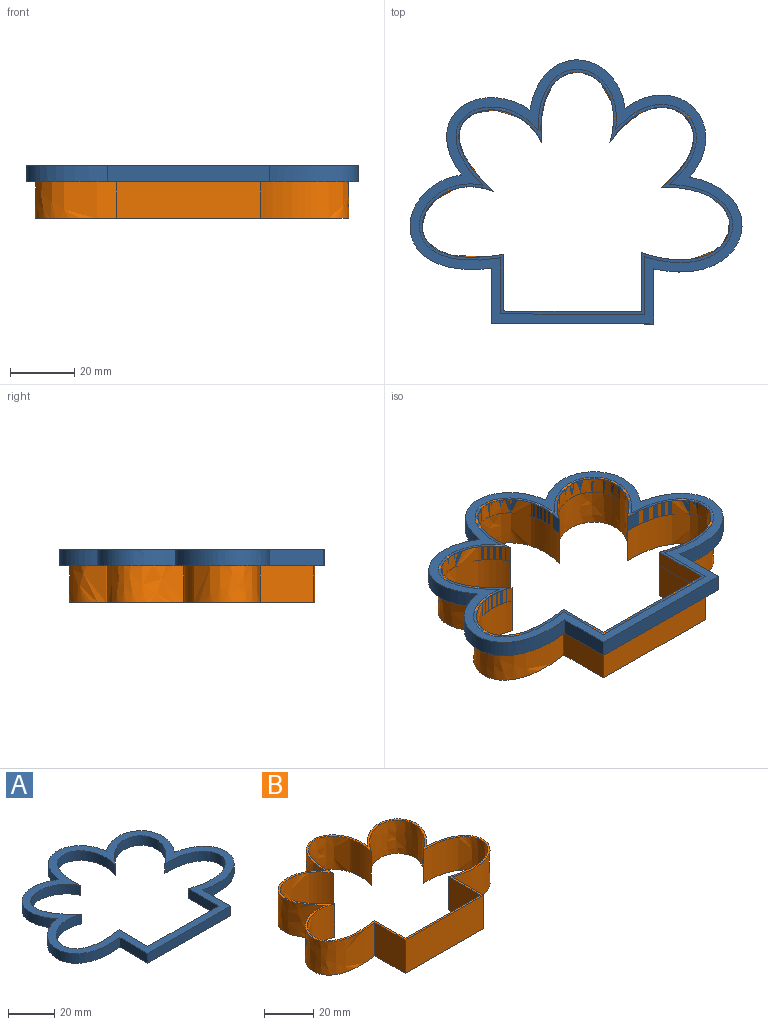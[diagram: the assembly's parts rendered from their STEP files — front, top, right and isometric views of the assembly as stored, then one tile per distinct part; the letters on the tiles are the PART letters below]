
ASSEMBLY  parts=2 mates=1
PART A: 18 faces, bbox 107.6x83.7x5.1 mm
  f0: plane 107.59x83.71mm, normal (0,0,1), area 1318.5mm2, adj f2,f3,f4,f5,f6,f7,f8,f9
  f1: plane 107.59x83.71mm, normal (0,0,-1), area 1318.5mm2, adj f2,f3,f4,f5,f6,f7,f8,f9
  f2: extruded ~29.44x25.38mm, area 290mm2, adj f0,f1,f3,f9
  f3: plane 17.02x5.08mm, normal (-1,0,0), area 86.4mm2, adj f0,f1,f2,f4
  f4: plane 50.51x5.08mm, normal (-0.01,-1,0), area 256.6mm2, adj f0,f1,f3,f5
  f5: plane 17.19x5.08mm, normal (1,0,0), area 87.3mm2, adj f0,f1,f4,f6
  f6: extruded ~29.53x27.52mm, area 300.9mm2, adj f0,f1,f5,f7
  f7: extruded ~25.58x25.16mm, area 239.9mm2, adj f0,f1,f6,f8
  f8: extruded ~29.6x15.62mm, area 236.6mm2, adj f0,f1,f7,f9
  f9: extruded ~25.96x24.12mm, area 236.6mm2, adj f0,f1,f2,f8
  f10: extruded ~25.38x21.98mm, area 300.8mm2, adj f0,f1,f11,f17
  f11: plane 17.61x5.08mm, normal (1,0,0), area 89.4mm2, adj f0,f1,f10,f12
  f12: plane 42.89x5.08mm, normal (0.01,1,0), area 217.9mm2, adj f0,f1,f11,f13
  f13: plane 18.41x5.08mm, normal (-1,0,0), area 93.5mm2, adj f0,f1,f12,f14
  f14: extruded ~27.52x22.61mm, area 305.9mm2, adj f0,f1,f13,f15
  f15: extruded ~26.04x24.88mm, area 277.7mm2, adj f0,f1,f14,f16
  f16: extruded ~22.61x21.8mm, area 280.9mm2, adj f0,f1,f15,f17
  f17: extruded ~25.72x25.41mm, area 279.6mm2, adj f0,f1,f10,f16
PART B: 18 faces, bbox 107.6x80.8x16.5 mm
  f0: plane 107.59x80.78mm, normal (0,0,1), area 316mm2, adj f2,f3,f4,f5,f6,f7,f8,f9
  f1: plane 107.59x80.78mm, normal (0,0,-1), area 316mm2, adj f2,f3,f4,f5,f6,f7,f8,f9
  f2: extruded ~25.4x23.77mm, area 949.7mm2, adj f0,f1,f3,f9
  f3: plane 17.44x16.51mm, normal (-1,0,0), area 288mm2, adj f0,f1,f2,f4
  f4: plane 44.67x16.51mm, normal (-0.01,-1,0), area 737.5mm2, adj f0,f1,f3,f5
  f5: plane 18.08x16.51mm, normal (1,0,0), area 298.4mm2, adj f0,f1,f4,f6
  f6: extruded ~27.52x24.36mm, area 982.6mm2, adj f0,f1,f5,f7
  f7: extruded ~25.19x24.9mm, area 843.1mm2, adj f0,f1,f6,f8
  f8: extruded ~24.41x19.21mm, area 837.5mm2, adj f0,f1,f7,f9
  f9: extruded ~25.53x24.35mm, area 837.3mm2, adj f0,f1,f2,f8
  f10: extruded ~25.38x21.98mm, area 977.7mm2, adj f0,f1,f11,f17
  f11: plane 17.61x16.51mm, normal (1,0,0), area 290.7mm2, adj f0,f1,f10,f12
  f12: plane 42.89x16.51mm, normal (0.01,1,0), area 708.1mm2, adj f0,f1,f11,f13
  f13: plane 18.41x16.51mm, normal (-1,0,0), area 304mm2, adj f0,f1,f12,f14
  f14: extruded ~27.52x22.61mm, area 994.3mm2, adj f0,f1,f13,f15
  f15: extruded ~26.04x24.88mm, area 902.4mm2, adj f0,f1,f14,f16
  f16: extruded ~22.61x21.8mm, area 912.9mm2, adj f0,f1,f15,f17
  f17: extruded ~25.72x25.41mm, area 908.8mm2, adj f0,f1,f10,f16
PLACE A at identity
PLACE B t=(105.06,-4.18,-11.43)mm
MATE fastened B.f0 <-> A.f0  axis (0,0,1) through (75.73,4.19,5.08)mm
